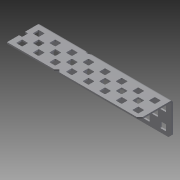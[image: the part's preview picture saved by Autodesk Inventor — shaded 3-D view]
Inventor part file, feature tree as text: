
AUTODESK INVENTOR PART (.ipt)
format: ipt  version: 2014 SP1 (Build 180222100, 222)  size: 911,872 bytes
history: native  units: in
note: dims shown in document units (in); Inventor stores cm internally (conversion verified against a paired STEP export)
features: other x1, imported_body x1, extrude x1, sketch x1
ambient origin geometry x8: Origin, YZ Plane, XZ Plane, XY Plane, X Axis, Y Axis, Z Axis, Center Point
bodies: Body1 (feature_tree)
feature tree (4):
  parser-record x1  (decoder bookkeeping rows leaked as tree rows — omitted from the tree; the rows remain in map.json)
  imported_body  "Base1"
  extrude  "Extrusion1"  Depth=3.5in
  sketch  "Sketch1"  dims[d0=1.0in d1=0.0in d2=3.5in]
